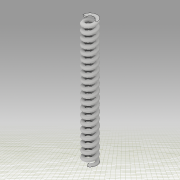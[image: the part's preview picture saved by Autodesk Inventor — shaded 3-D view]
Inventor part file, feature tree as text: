
AUTODESK INVENTOR PART (.ipt)
format: ipt  version: 2018 (Build 220112000, 112)  size: 626,688 bytes
history: native  units: in
note: dims shown in document units (in); Inventor stores cm internally (conversion verified against a paired STEP export)
features: sketch x2, helix x1, extrude x1
ambient origin geometry x8: Origin, YZ Plane, XZ Plane, XY Plane, X Axis, Y Axis, Z Axis, Center Point
bodies: Solid1 (feature_tree)
feature tree (4):
  helix  "Coil1"  [1 undecoded]
  extrude  "Extrusion2"  Depth=1.0in TaperAngle=0.0deg
  sketch  "Sketch1"  dims[d1=0.0531in]
  sketch  "Sketch2"  dims[d2=1.0in d3=0.926in d4=7.874in d5=0.0in d6=90.0deg d7=30.0deg d8=90.0deg d9=30.0deg d12=1.0in d13=0.0in]
note: 1 required parameter value undecoded (feature->parameter linkage not recoverable at this tier; creation-order binding heuristic only, values carry confidence <= 0.55)
